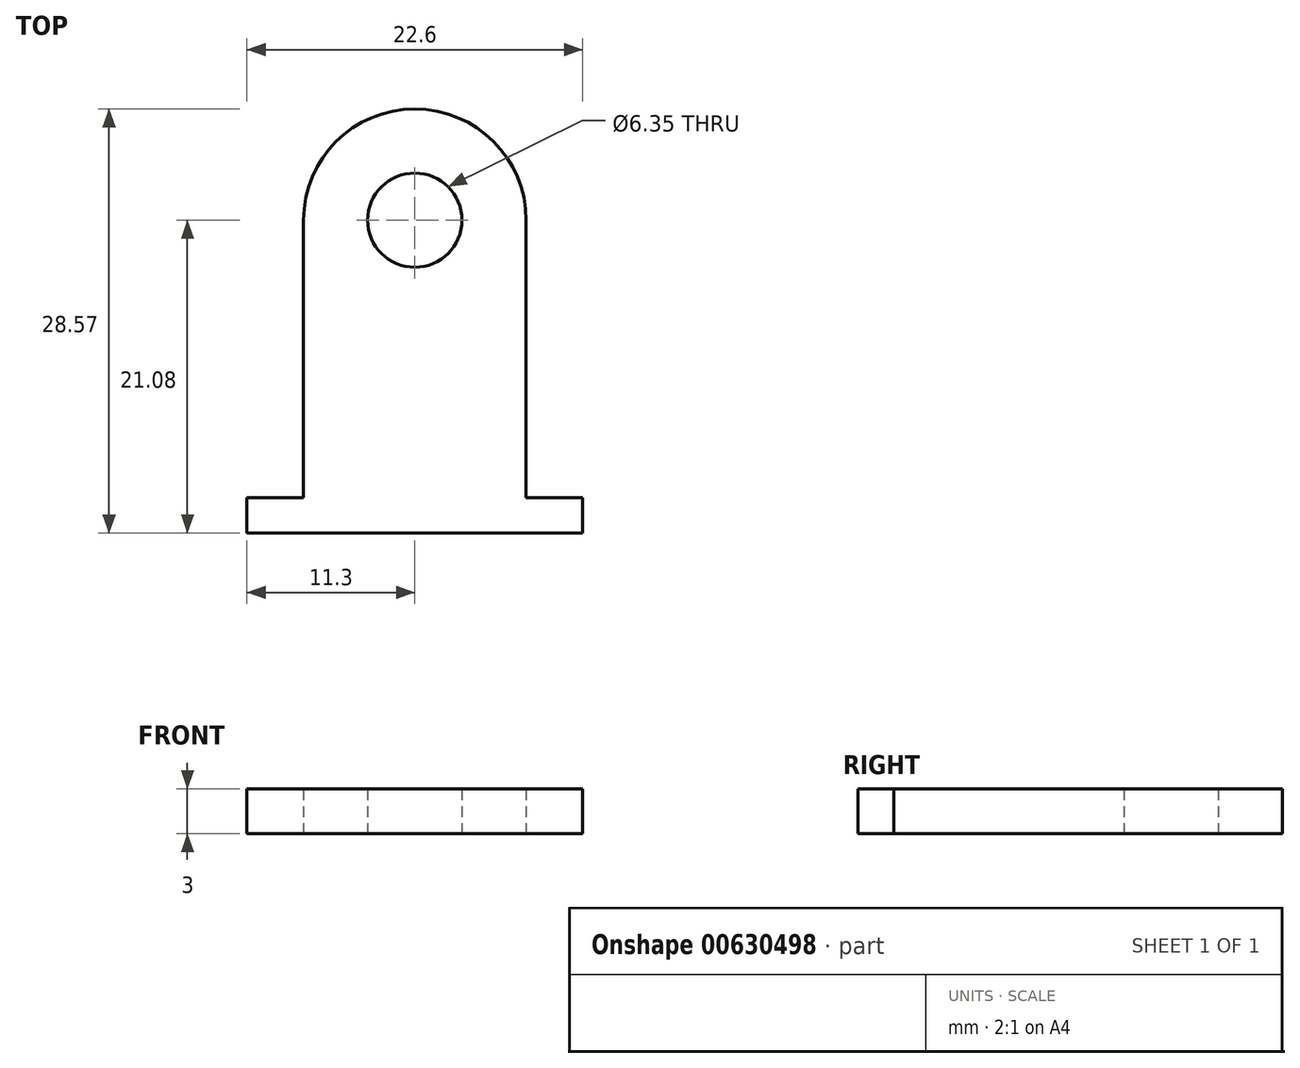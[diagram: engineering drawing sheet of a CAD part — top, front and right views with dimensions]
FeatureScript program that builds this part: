
annotation { "Feature Type Name" : "Feature", "Feature Type Description" : "" }
export const myFeature = defineFeature(function(context is Context, id is Id, definition is map)
    precondition{}
    {
        {
            var Q0;
            Q0=qCreatedBy(makeId("Top.planeOp"),FACE);
            var sketch = newSketch(context, id + "F0", { "sketchPlane" : qUnion([Q0])});
            skLineSegment(sketch, "E0.left", {"start": v(-7.5, 0) * mm, "end": v(-7.5, -18.7) * mm});
            skLineSegment(sketch, "E0.right", {"start": v(7.5, 0) * mm, "end": v(7.5, -18.7) * mm});
            skLineSegment(sketch, "E1.bottom", {"start": v(-11.3, -18.7) * mm, "end": v(-7.5, -18.7) * mm});
            skLineSegment(sketch, "E1.top", {"start": v(-11.3, -21.08) * mm, "end": v(11.3, -21.08) * mm});
            skLineSegment(sketch, "E1.left", {"start": v(-11.3, -18.7) * mm, "end": v(-11.3, -21.08) * mm});
            skLineSegment(sketch, "E1.right", {"start": v(11.3, -18.7) * mm, "end": v(11.3, -21.08) * mm});
            skLineSegment(sketch, "E2.trimOffspring", {"start": v(7.5, -18.7) * mm, "end": v(11.3, -18.7) * mm});
            skArc(sketch, "E3", {"start": v(7.5, 0) * mm, "mid": v(0, 7.5) * mm, "end": v(-7.5, 0) * mm});
            skCircle(sketch, "E4", {"center": v(0, 0) * mm, "radius": 3.18 * mm});
            skLineSegment(sketch, "E5", {"start": v(7.5, 0) * mm, "end": v(-7.5, 0) * mm});
            skSolve(sketch);
        }
        {
            var Q0;
            Q0=qSketchRegion(id+"F0",true);
            extrude(context, id + "F1", {"entities" : qUnion([Q0]), "depth" : 3 * mm, "offsetDistance" : 25.4 * mm});
        }
    });
